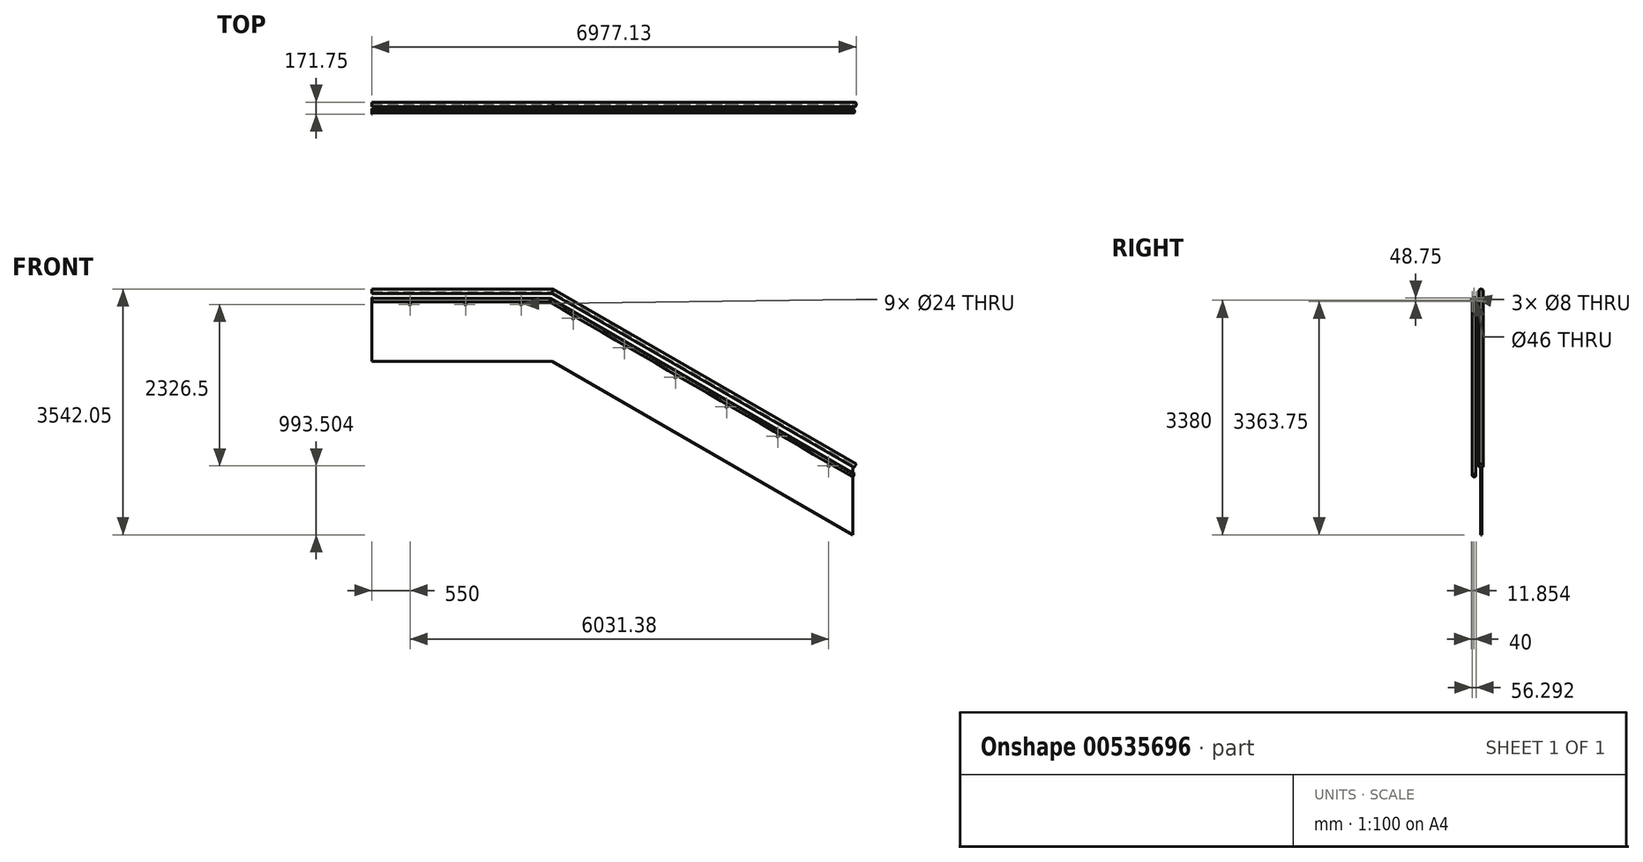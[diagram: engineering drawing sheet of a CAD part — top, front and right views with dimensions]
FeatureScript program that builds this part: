
annotation { "Feature Type Name" : "Feature", "Feature Type Description" : "" }
export const myFeature = defineFeature(function(context is Context, id is Id, definition is map)
    precondition{}
    {
        {
            var Q0;
            Q0=qCreatedBy(makeId("Front.planeOp"),FACE);
            var sketch = newSketch(context, id + "F0", { "sketchPlane" : qUnion([Q0])});
            skLineSegment(sketch, "E0.bottom", {"start": v(0, 0) * mm, "end": v(2600, 0) * mm});
            skLineSegment(sketch, "E0.top", {"start": v(0, 1000) * mm, "end": v(2600, 1000) * mm});
            skLineSegment(sketch, "E0.left", {"start": v(0, 0) * mm, "end": v(0, 1000) * mm});
            skLineSegment(sketch, "E1", {"start": v(2600, 0) * mm, "end": v(6930.13, -2500) * mm});
            skLineSegment(sketch, "E2", {"start": v(6930.13, -2500) * mm, "end": v(6930.13, -1500) * mm});
            skLineSegment(sketch, "E3", {"start": v(6930.13, -1500) * mm, "end": v(2600, 1000) * mm});
            skLineSegment(sketch, "E4.0", {"start": v(6930.13, -1707.85) * mm, "end": v(2551.77, 820) * mm, "construction": true});
            skLineSegment(sketch, "E4.1", {"start": v(0, 820) * mm, "end": v(2551.77, 820) * mm, "construction": true});
            skCircle(sketch, "E5", {"center": v(550, 820) * mm, "radius": 12 * mm});
            skCircle(sketch, "E6", {"center": v(2150, 820) * mm, "radius": 12 * mm});
            skCircle(sketch, "E7", {"center": v(2900.78, 618.5) * mm, "radius": 12 * mm});
            skCircle(sketch, "E8", {"center": v(5845.26, -1081.5) * mm, "radius": 12 * mm});
            skCircle(sketch, "E9", {"center": v(6581.38, -1506.5) * mm, "radius": 12 * mm});
            skCircle(sketch, "E10", {"center": v(3636.9, 193.5) * mm, "radius": 12 * mm});
            skCircle(sketch, "E11", {"center": v(4373.01, -231.5) * mm, "radius": 12 * mm});
            skCircle(sketch, "E12", {"center": v(5109.14, -656.5) * mm, "radius": 12 * mm});
            skCircle(sketch, "E13", {"center": v(1350, 820) * mm, "radius": 12 * mm});
            skSolve(sketch);
        }
        {
            var Q0;
            Q0=qSketchRegion(id+"F0",true);
            extrude(context, id + "F1", {"entities" : qUnion([Q0]), "endBound" : BoundingType.SYMMETRIC, "depth" : 19 * mm, "offsetDistance" : 25 * mm});
        }
        {
            var Q0;
            Q0=qCreatedBy(makeId("Front.planeOp"),FACE);
            var sketch = newSketch(context, id + "F2", { "sketchPlane" : qUnion([Q0])});
            skLineSegment(sketch, "E14.0", {"start": v(0, 1000) * mm, "end": v(2600, 1000) * mm});
            skLineSegment(sketch, "E14.1", {"start": v(6956.1, -1515) * mm, "end": v(2600, 1000) * mm});
            skSolve(sketch);
        }
        {
            var Q0;
            Q0=qCreatedBy(makeId("Right.planeOp"),FACE);
            var sketch = newSketch(context, id + "F3", { "sketchPlane" : qUnion([Q0])});
            skLineSegment(sketch, "E15", {"start": v(9.5, 980) * mm, "end": v(9.5, 1000) * mm});
            skLineSegment(sketch, "E16.0", {"start": v(-9.5, 1000) * mm, "end": v(9.5, 1000) * mm});
            skLineSegment(sketch, "E17", {"start": v(-9.5, 1000) * mm, "end": v(-9.5, 980) * mm});
            skArc(sketch, "E18", {"start": v(9.5, 980) * mm, "mid": v(0, 1042.05) * mm, "end": v(-9.5, 980) * mm});
            skArc(sketch, "E19.0", {"start": v(11, 982.12) * mm, "mid": v(0, 1040.55) * mm, "end": v(-11, 982.12) * mm});
            skLineSegment(sketch, "E19.1", {"start": v(11, 982.12) * mm, "end": v(11, 1001.5) * mm});
            skLineSegment(sketch, "E19.2", {"start": v(-11, 1001.5) * mm, "end": v(11, 1001.5) * mm});
            skLineSegment(sketch, "E19.3", {"start": v(-11, 1001.5) * mm, "end": v(-11, 982.12) * mm});
            skSolve(sketch);
        }
        {
            var Q0;
            Q0=qSketchRegion(id+"F3",true);
            var Q1;
            Q1=sQuery(id+"F2.wireOp",EDGE,"E14.0");
            var Q2;
            Q2=sQuery(id+"F2.wireOp",EDGE,"E14.1");
            sweep(context, id + "F4", {"profiles" : qUnion([Q0]), "path" : qUnion([Q1, Q2])});
        }
        {
            var Q0;
            Q0=makeQuery(id+"F4.opSweep","CAP_FACE",FACE,{"disambiguationData":[OSD([sQuery(id+"F2.wireOp",VERTEX,"E14.1.start"),sQuery(id+"F3.wireOp",EDGE,"E15"),sQuery(id+"F3.wireOp",EDGE,"E16.0"),sQuery(id+"F3.wireOp",EDGE,"E17"),sQuery(id+"F3.wireOp",EDGE,"E18"),sQuery(id+"F3.wireOp",EDGE,"E19.0"),sQuery(id+"F3.wireOp",EDGE,"E19.1"),sQuery(id+"F3.wireOp",EDGE,"E19.2"),sQuery(id+"F3.wireOp",EDGE,"E19.3")])],"isStart":false});
            var sketch = newSketch(context, id + "F5", { "sketchPlane" : qUnion([Q0])});
            skCircle(sketch, "E20", {"center": v(0, 2176.32) * mm, "radius": 31.75 * mm});
            skSolve(sketch);
        }
        {
            var Q0;
            Q0=qSketchRegion(id+"F5",true);
            extrude(context, id + "F6", {"entities" : qUnion([Q0]), "operationType" : NewBodyOperationType.ADD, "oppositeDirection" : true, "depth" : 2 * mm, "offsetDistance" : 25 * mm});
        }
        {
            var Q0;
            Q0=qCreatedBy(makeId("Front.planeOp"),FACE);
            cPlane(context, id + "F7", {"entities" : qUnion([Q0]), "cplaneType" : CPlaneType.OFFSET, "offset" : 100 * mm, "width" : 150 * mm, "height" : 150 * mm});
        }
        {
            var Q0;
            Q0=qCreatedBy(id+"F7.planeOp",FACE);
            var sketch = newSketch(context, id + "F8", { "sketchPlane" : qUnion([Q0])});
            skLineSegment(sketch, "E21.0", {"start": v(2567.85, 880) * mm, "end": v(6941.27, -1645) * mm});
            skLineSegment(sketch, "E21.1", {"start": v(0, 880) * mm, "end": v(2567.85, 880) * mm});
            skSolve(sketch);
        }
        {
            var Q0;
            Q0=qCreatedBy(makeId("Right.planeOp"),FACE);
            var sketch = newSketch(context, id + "F9", { "sketchPlane" : qUnion([Q0])});
            skCircle(sketch, "E22", {"center": v(-100, 880) * mm, "radius": 25 * mm});
            skCircle(sketch, "E23.0", {"center": v(-100, 880) * mm, "radius": 23 * mm});
            skSolve(sketch);
        }
        {
            var Q0;
            Q0=makeQuery(id+"F9.imprint","IMPRINT",FACE,{"disambiguationData":[TD([[makeQuery(id+"F9.imprint","IMPRINT",EDGE,{"derivedFrom":sQuery(id+"F9.wireOp",EDGE,"E22")}),1.0]])]});
            var Q1;
            Q1=sQuery(id+"F8.wireOp",EDGE,"E21.1");
            var Q2;
            Q2=sQuery(id+"F8.wireOp",EDGE,"E21.0");
            sweep(context, id + "F10", {"profiles" : qUnion([Q0]), "path" : qUnion([Q1, Q2])});
        }
        {
            var Q0;
            Q0=qCreatedBy(id+"F7.planeOp",FACE);
            var sketch = newSketch(context, id + "F11", { "sketchPlane" : qUnion([Q0])});
            skLineSegment(sketch, "E24.0", {"start": v(6953.77, -1623.35) * mm, "end": v(6941.27, -1645) * mm});
            skLineSegment(sketch, "E25", {"start": v(6941.27, -1645) * mm, "end": v(6962.93, -1657.5) * mm});
            skArc(sketch, "E26", {"start": v(6953.77, -1623.35) * mm, "mid": v(6965.42, -1638.53) * mm, "end": v(6962.93, -1657.5) * mm});
            skLineSegment(sketch, "E27", {"start": v(3457.45, 366.39) * mm, "end": v(6941.27, -1645) * mm, "construction": true});
            skPoint(sketch, "E28.orphan", {"position": v(6928.77, -1666.65) * mm});
            skSolve(sketch);
        }
        {
            var Q0;
            Q0=makeQuery(id+"F10.opSweep","CAP_FACE",FACE,{"disambiguationData":[OSD([sQuery(id+"F8.wireOp",VERTEX,"E21.0.end"),sQuery(id+"F9.wireOp",EDGE,"E22"),sQuery(id+"F9.wireOp",EDGE,"E23.0")])],"isStart":false});
            var sketch = newSketch(context, id + "F12", { "sketchPlane" : qUnion([Q0])});
            skCircle(sketch, "E29", {"center": v(-100, 2046.03) * mm, "radius": 25 * mm});
            skSolve(sketch);
        }
        {
            var Q0;
            Q0=qSketchRegion(id+"F12",true);
            extrude(context, id + "F13", {"entities" : qUnion([Q0]), "operationType" : NewBodyOperationType.ADD, "oppositeDirection" : true, "depth" : 3 * mm, "offsetDistance" : 25 * mm});
        }
        {
            var Q0;
            Q0=makeQuery(id+"F10.opSweep","CAP_FACE",FACE,{"disambiguationData":[OSD([sQuery(id+"F8.wireOp",VERTEX,"E21.1.start"),sQuery(id+"F9.wireOp",EDGE,"E22"),sQuery(id+"F9.wireOp",EDGE,"E23.0")])],"isStart":true});
            var sketch = newSketch(context, id + "F14", { "sketchPlane" : qUnion([Q0])});
            skCircle(sketch, "E30.0", {"center": v(100, 880) * mm, "radius": 25 * mm});
            skCircle(sketch, "E31.0", {"center": v(100, 880) * mm, "radius": 40 * mm});
            skCircle(sketch, "E32", {"center": v(100, 912.5) * mm, "radius": 4 * mm});
            skCircle(sketch, "E33", {"center": v(128.15, 863.75) * mm, "radius": 4 * mm});
            skCircle(sketch, "E34", {"center": v(71.85, 863.75) * mm, "radius": 4 * mm});
            skCircle(sketch, "E35", {"center": v(100, 880) * mm, "radius": 32.5 * mm, "construction": true});
            skLineSegment(sketch, "E36", {"start": v(100, 880) * mm, "end": v(128.15, 863.75) * mm, "construction": true});
            skLineSegment(sketch, "E37", {"start": v(100, 880) * mm, "end": v(71.85, 863.75) * mm, "construction": true});
            skLineSegment(sketch, "E38", {"start": v(100, 880) * mm, "end": v(100, 912.5) * mm, "construction": true});
            skSolve(sketch);
        }
        {
            var Q0;
            Q0=makeQuery(id+"F14.imprint","IMPRINT",FACE,{"disambiguationData":[TD([[makeQuery(id+"F14.imprint","IMPRINT",EDGE,{"derivedFrom":sQuery(id+"F14.wireOp",EDGE,"E30.0")}),1.0]])]});
            extrude(context, id + "F15", {"entities" : qUnion([Q0]), "operationType" : NewBodyOperationType.ADD, "oppositeDirection" : true, "depth" : 5 * mm, "offsetDistance" : 25 * mm});
        }
    });
